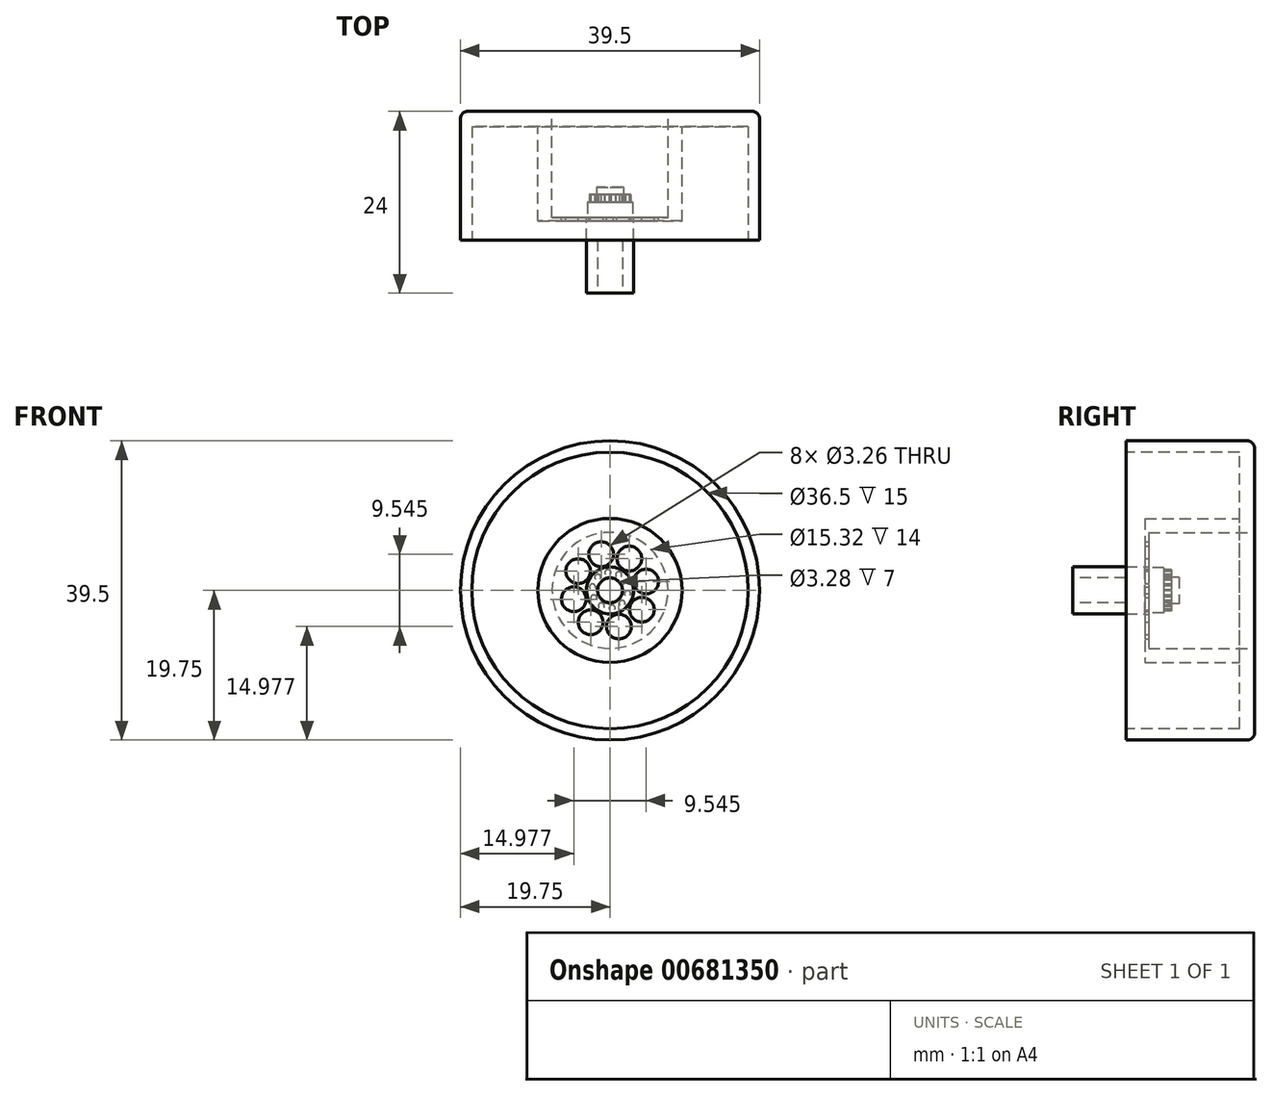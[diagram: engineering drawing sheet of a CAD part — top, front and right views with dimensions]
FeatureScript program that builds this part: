
annotation { "Feature Type Name" : "Feature", "Feature Type Description" : "" }
export const myFeature = defineFeature(function(context is Context, id is Id, definition is map)
    precondition{}
    {
        {
            var Q0;
            Q0=qCreatedBy(makeId("Front.planeOp"),FACE);
            var sketch = newSketch(context, id + "F0", { "sketchPlane" : qUnion([Q0])});
            skCircle(sketch, "E0", {"center": v(0, 0) * mm, "radius": 19.75 * mm});
            skSolve(sketch);
        }
        {
            var Q0;
            Q0 = qSketchRegion(id + "F0", true);
            extrude(context, id + "F1", {"entities" : qUnion([Q0]), "depth" : 17 * mm, "offsetDistance" : 25.4 * mm});
        }
        {
            var Q0;
            Q0=makeQuery(id+"F1.opExtrude","CAP_FACE",FACE,{"disambiguationData":[OSD([sQuery(id+"F0.wireOp",EDGE,"E0")])],"isStart":false});
            var sketch = newSketch(context, id + "F2", { "sketchPlane" : qUnion([Q0])});
            skCircle(sketch, "E1", {"center": v(0, 0) * mm, "radius": 18.25 * mm});
            skSolve(sketch);
        }
        {
            var Q0;
            Q0 = qSketchRegion(id + "F2", true);
            extrude(context, id + "F3", {"entities" : qUnion([Q0]), "operationType" : NewBodyOperationType.REMOVE, "oppositeDirection" : true, "depth" : 15 * mm, "offsetDistance" : 25.4 * mm});
        }
        {
            var Q0;
            Q0=makeQuery(id+"F1.opExtrude","CAP_FACE",FACE,{"disambiguationData":[OSD([sQuery(id+"F0.wireOp",EDGE,"E0")])],"isStart":true});
            var sketch = newSketch(context, id + "F4", { "sketchPlane" : qUnion([Q0])});
            skCircle(sketch, "E2", {"center": v(0, 0) * mm, "radius": 9.5 * mm});
            skSolve(sketch);
        }
        {
            var Q0;
            Q0=makeQuery(id+"F4.imprint","IMPRINT",FACE,{"disambiguationData":[TD([[makeQuery(id+"F4.imprint","IMPRINT",EDGE,{"derivedFrom":sQuery(id+"F4.wireOp",EDGE,"E2")}),1.0]])]});
            extrude(context, id + "F5", {"entities" : qUnion([Q0]), "operationType" : NewBodyOperationType.ADD, "oppositeDirection" : true, "depth" : 14.5 * mm, "offsetDistance" : 25.4 * mm});
        }
        {
            var Q0;
            Q0=makeQuery(id+"F1.opExtrude","CAP_FACE",FACE,{"disambiguationData":[OSD([sQuery(id+"F0.wireOp",EDGE,"E0")])],"isStart":true});
            var sketch = newSketch(context, id + "F6", { "sketchPlane" : qUnion([Q0])});
            skCircle(sketch, "E3", {"center": v(0, 0) * mm, "radius": 7.66 * mm});
            skSolve(sketch);
        }
        {
            var Q0;
            Q0=makeQuery(id+"F6.imprint","IMPRINT",FACE,{"disambiguationData":[TD([[makeQuery(id+"F6.imprint","IMPRINT",EDGE,{"derivedFrom":sQuery(id+"F6.wireOp",EDGE,"E3")}),1.0]])]});
            extrude(context, id + "F7", {"entities" : qUnion([Q0]), "operationType" : NewBodyOperationType.REMOVE, "oppositeDirection" : true, "depth" : 14 * mm, "offsetDistance" : 25.4 * mm});
        }
        {
            var Q0;
            Q0=makeQuery(id+"F5.opExtrude","CAP_FACE",FACE,{"disambiguationData":[OSD([sQuery(id+"F4.wireOp",EDGE,"E2")])],"isStart":false});
            var sketch = newSketch(context, id + "F8", { "sketchPlane" : qUnion([Q0])});
            skCircle(sketch, "E4", {"center": v(0, 0) * mm, "radius": 3.1 * mm});
            skSolve(sketch);
        }
        {
            var Q0;
            Q0=makeQuery(id+"F8.imprint","IMPRINT",FACE,{"disambiguationData":[TD([[makeQuery(id+"F8.imprint","IMPRINT",EDGE,{"derivedFrom":sQuery(id+"F8.wireOp",EDGE,"E4")}),1.0]])]});
            extrude(context, id + "F9", {"entities" : qUnion([Q0]), "operationType" : NewBodyOperationType.ADD, "depth" : 9.5 * mm, "offsetDistance" : 25.4 * mm});
        }
        {
            var Q0;
            Q0=makeQuery(id+"F9.opExtrude","CAP_FACE",FACE,{"disambiguationData":[OSD([sQuery(id+"F8.wireOp",EDGE,"E4")])],"isStart":false});
            var sketch = newSketch(context, id + "F10", { "sketchPlane" : qUnion([Q0])});
            skCircle(sketch, "E5", {"center": v(0, 0) * mm, "radius": 1.64 * mm});
            skSolve(sketch);
        }
        {
            var Q0;
            Q0=makeQuery(id+"F10.imprint","IMPRINT",FACE,{"disambiguationData":[TD([[makeQuery(id+"F10.imprint","IMPRINT",EDGE,{"derivedFrom":sQuery(id+"F10.wireOp",EDGE,"E5")}),1.0]])]});
            extrude(context, id + "F11", {"entities" : qUnion([Q0]), "operationType" : NewBodyOperationType.REMOVE, "oppositeDirection" : true, "depth" : 7 * mm, "offsetDistance" : 25.4 * mm});
        }
        {
            var Q0;
            Q0=makeQuery(id+"F7.boolean.opBoolean","COPY",FACE,{"derivedFrom":makeQuery(id+"F7.opExtrude","CAP_FACE",FACE,{"disambiguationData":[OSD([sQuery(id+"F6.wireOp",EDGE,"E3")])],"isStart":false})});
            var sketch = newSketch(context, id + "F12", { "sketchPlane" : qUnion([Q0])});
            skCircle(sketch, "E6", {"center": v(-2.55, 4.2) * mm, "radius": 1.63 * mm});
            skCircle(sketch, "E7.1.0", {"center": v(-4.77, 1.17) * mm, "radius": 1.63 * mm});
            skCircle(sketch, "E7.2.0", {"center": v(-4.2, -2.55) * mm, "radius": 1.63 * mm});
            skCircle(sketch, "E7.3.0", {"center": v(-1.17, -4.77) * mm, "radius": 1.63 * mm});
            skCircle(sketch, "E7.4.0", {"center": v(2.55, -4.2) * mm, "radius": 1.63 * mm});
            skCircle(sketch, "E7.5.0", {"center": v(4.77, -1.17) * mm, "radius": 1.63 * mm});
            skCircle(sketch, "E7.6.0", {"center": v(4.2, 2.55) * mm, "radius": 1.63 * mm});
            skCircle(sketch, "E7.7.0", {"center": v(1.17, 4.77) * mm, "radius": 1.63 * mm});
            skPoint(sketch, "E7.center", {"position": v(0, 0) * mm});
            skSolve(sketch);
        }
        {
            var Q0;
            Q0=makeQuery(id+"F12.imprint","IMPRINT",FACE,{"disambiguationData":[TD([[makeQuery(id+"F12.imprint","IMPRINT",EDGE,{"derivedFrom":sQuery(id+"F12.wireOp",EDGE,"E6")}),1.0]])]});
            var Q1;
            Q1=makeQuery(id+"F12.imprint","IMPRINT",FACE,{"disambiguationData":[TD([[makeQuery(id+"F12.imprint","IMPRINT",EDGE,{"derivedFrom":sQuery(id+"F12.wireOp",EDGE,"E7.7.0")}),1.0]])]});
            var Q2;
            Q2=makeQuery(id+"F12.imprint","IMPRINT",FACE,{"disambiguationData":[TD([[makeQuery(id+"F12.imprint","IMPRINT",EDGE,{"derivedFrom":sQuery(id+"F12.wireOp",EDGE,"E7.6.0")}),1.0]])]});
            var Q3;
            Q3=makeQuery(id+"F12.imprint","IMPRINT",FACE,{"disambiguationData":[TD([[makeQuery(id+"F12.imprint","IMPRINT",EDGE,{"derivedFrom":sQuery(id+"F12.wireOp",EDGE,"E7.5.0")}),1.0]])]});
            var Q4;
            Q4=makeQuery(id+"F12.imprint","IMPRINT",FACE,{"disambiguationData":[TD([[makeQuery(id+"F12.imprint","IMPRINT",EDGE,{"derivedFrom":sQuery(id+"F12.wireOp",EDGE,"E7.4.0")}),1.0]])]});
            var Q5;
            Q5=makeQuery(id+"F12.imprint","IMPRINT",FACE,{"disambiguationData":[TD([[makeQuery(id+"F12.imprint","IMPRINT",EDGE,{"derivedFrom":sQuery(id+"F12.wireOp",EDGE,"E7.3.0")}),1.0]])]});
            var Q6;
            Q6=makeQuery(id+"F12.imprint","IMPRINT",FACE,{"disambiguationData":[TD([[makeQuery(id+"F12.imprint","IMPRINT",EDGE,{"derivedFrom":sQuery(id+"F12.wireOp",EDGE,"E7.2.0")}),1.0]])]});
            var Q7;
            Q7=makeQuery(id+"F12.imprint","IMPRINT",FACE,{"disambiguationData":[TD([[makeQuery(id+"F12.imprint","IMPRINT",EDGE,{"derivedFrom":sQuery(id+"F12.wireOp",EDGE,"E7.1.0")}),1.0]])]});
            extrude(context, id + "F13", {"entities" : qUnion([Q0, Q1, Q2, Q3, Q4, Q5, Q6, Q7]), "operationType" : NewBodyOperationType.REMOVE, "oppositeDirection" : true, "depth" : 25.4 * mm, "offsetDistance" : 25.4 * mm});
        }
        {
            var Q0;
            Q0=makeQuery(id+"F7.boolean.opBoolean","COPY",FACE,{"derivedFrom":makeQuery(id+"F7.opExtrude","CAP_FACE",FACE,{"disambiguationData":[OSD([sQuery(id+"F6.wireOp",EDGE,"E3")])],"isStart":false})});
            var sketch = newSketch(context, id + "F14", { "sketchPlane" : qUnion([Q0])});
            skCircle(sketch, "E8", {"center": v(0, 0) * mm, "radius": 3 * mm});
            skSolve(sketch);
        }
        {
            var Q0;
            Q0=makeQuery(id+"F14.imprint","IMPRINT",FACE,{"disambiguationData":[TD([[makeQuery(id+"F14.imprint","IMPRINT",EDGE,{"derivedFrom":sQuery(id+"F14.wireOp",EDGE,"E8")}),1.0]])]});
            var Q1;
            Q1=sQuery(id+"F14.wireOp",EDGE,"E8");
            extrude(context, id + "F15", {"entities" : qUnion([Q0]), "operationType" : NewBodyOperationType.ADD, "surfaceEntities" : qUnion([Q1]), "depth" : 2 * mm, "offsetDistance" : 25.4 * mm});
        }
        {
            var Q0;
            Q0=makeQuery(id+"F15.opExtrude","CAP_FACE",FACE,{"disambiguationData":[OSD([sQuery(id+"F14.wireOp",EDGE,"E8")])],"isStart":false});
            var sketch = newSketch(context, id + "F16", { "sketchPlane" : qUnion([Q0])});
            skCircle(sketch, "E9", {"center": v(0, 0) * mm, "radius": 1.75 * mm});
            skSolve(sketch);
        }
        {
            var Q0;
            Q0=makeQuery(id+"F16.imprint","IMPRINT",FACE,{"disambiguationData":[TD([[makeQuery(id+"F16.imprint","IMPRINT",EDGE,{"derivedFrom":sQuery(id+"F16.wireOp",EDGE,"E9")}),1.0]])]});
            extrude(context, id + "F17", {"entities" : qUnion([Q0]), "operationType" : NewBodyOperationType.ADD, "depth" : 2 * mm, "offsetDistance" : 25.4 * mm});
        }
        {
            var Q0;
            Q0=makeQuery(id+"F15.opExtrude","CAP_FACE",FACE,{"disambiguationData":[OSD([sQuery(id+"F14.wireOp",EDGE,"E8")])],"isStart":false});
            var sketch = newSketch(context, id + "F18", { "sketchPlane" : qUnion([Q0])});
            skCircle(sketch, "E10", {"center": v(-1.14, 2.06) * mm, "radius": 0.4 * mm});
            skCircle(sketch, "E11.1.0", {"center": v(-2.14, 1) * mm, "radius": 0.4 * mm});
            skCircle(sketch, "E11.2.0", {"center": v(-2.31, -0.45) * mm, "radius": 0.4 * mm});
            skCircle(sketch, "E11.3.0", {"center": v(-1.6, -1.72) * mm, "radius": 0.4 * mm});
            skCircle(sketch, "E11.4.0", {"center": v(-0.29, -2.34) * mm, "radius": 0.4 * mm});
            skCircle(sketch, "E11.5.0", {"center": v(1.14, -2.06) * mm, "radius": 0.4 * mm});
            skCircle(sketch, "E11.6.0", {"center": v(2.14, -1) * mm, "radius": 0.4 * mm});
            skCircle(sketch, "E11.7.0", {"center": v(2.31, 0.45) * mm, "radius": 0.4 * mm});
            skCircle(sketch, "E11.8.0", {"center": v(1.6, 1.72) * mm, "radius": 0.4 * mm});
            skCircle(sketch, "E11.9.0", {"center": v(0.29, 2.34) * mm, "radius": 0.4 * mm});
            skPoint(sketch, "E11.center", {"position": v(0, 0) * mm});
            skSolve(sketch);
        }
        {
            var Q0;
            Q0=makeQuery(id+"F18.imprint","IMPRINT",FACE,{"disambiguationData":[TD([[makeQuery(id+"F18.imprint","IMPRINT",EDGE,{"derivedFrom":sQuery(id+"F18.wireOp",EDGE,"E11.9.0")}),1.0]])]});
            var Q1;
            Q1=makeQuery(id+"F18.imprint","IMPRINT",FACE,{"disambiguationData":[TD([[makeQuery(id+"F18.imprint","IMPRINT",EDGE,{"derivedFrom":sQuery(id+"F18.wireOp",EDGE,"E11.8.0")}),1.0]])]});
            var Q2;
            Q2=makeQuery(id+"F18.imprint","IMPRINT",FACE,{"disambiguationData":[TD([[makeQuery(id+"F18.imprint","IMPRINT",EDGE,{"derivedFrom":sQuery(id+"F18.wireOp",EDGE,"E11.7.0")}),1.0]])]});
            var Q3;
            Q3=makeQuery(id+"F18.imprint","IMPRINT",FACE,{"disambiguationData":[TD([[makeQuery(id+"F18.imprint","IMPRINT",EDGE,{"derivedFrom":sQuery(id+"F18.wireOp",EDGE,"E11.6.0")}),1.0]])]});
            var Q4;
            Q4=makeQuery(id+"F18.imprint","IMPRINT",FACE,{"disambiguationData":[TD([[makeQuery(id+"F18.imprint","IMPRINT",EDGE,{"derivedFrom":sQuery(id+"F18.wireOp",EDGE,"E11.5.0")}),1.0]])]});
            var Q5;
            Q5=makeQuery(id+"F18.imprint","IMPRINT",FACE,{"disambiguationData":[TD([[makeQuery(id+"F18.imprint","IMPRINT",EDGE,{"derivedFrom":sQuery(id+"F18.wireOp",EDGE,"E11.4.0")}),1.0]])]});
            var Q6;
            Q6=makeQuery(id+"F18.imprint","IMPRINT",FACE,{"disambiguationData":[TD([[makeQuery(id+"F18.imprint","IMPRINT",EDGE,{"derivedFrom":sQuery(id+"F18.wireOp",EDGE,"E11.2.0")}),1.0]])]});
            var Q7;
            Q7=makeQuery(id+"F18.imprint","IMPRINT",FACE,{"disambiguationData":[TD([[makeQuery(id+"F18.imprint","IMPRINT",EDGE,{"derivedFrom":sQuery(id+"F18.wireOp",EDGE,"E10")}),1.0]])]});
            var Q8;
            Q8=makeQuery(id+"F18.imprint","IMPRINT",FACE,{"disambiguationData":[TD([[makeQuery(id+"F18.imprint","IMPRINT",EDGE,{"derivedFrom":sQuery(id+"F18.wireOp",EDGE,"E11.1.0")}),1.0]])]});
            var Q9;
            Q9=makeQuery(id+"F18.imprint","IMPRINT",FACE,{"disambiguationData":[TD([[makeQuery(id+"F18.imprint","IMPRINT",EDGE,{"derivedFrom":sQuery(id+"F18.wireOp",EDGE,"E11.3.0")}),1.0]])]});
            extrude(context, id + "F19", {"entities" : qUnion([Q0, Q1, Q2, Q3, Q4, Q5, Q6, Q7, Q8, Q9]), "operationType" : NewBodyOperationType.ADD, "depth" : 1 * mm, "offsetDistance" : 25.4 * mm});
        }
        {
            var Q0;
            Q0=makeQuery(id+"F1.opExtrude","CAP_EDGE",EDGE,{"disambiguationData":[OSD([sQuery(id+"F0.wireOp",EDGE,"E0")])],"isStart":true});
            fillet(context, id + "F20", {"entities" : qUnion([Q0]), "radius" : 1 * mm, "tangentPropagation" : true, "allowEdgeOverflow" : false});
        }
    });
